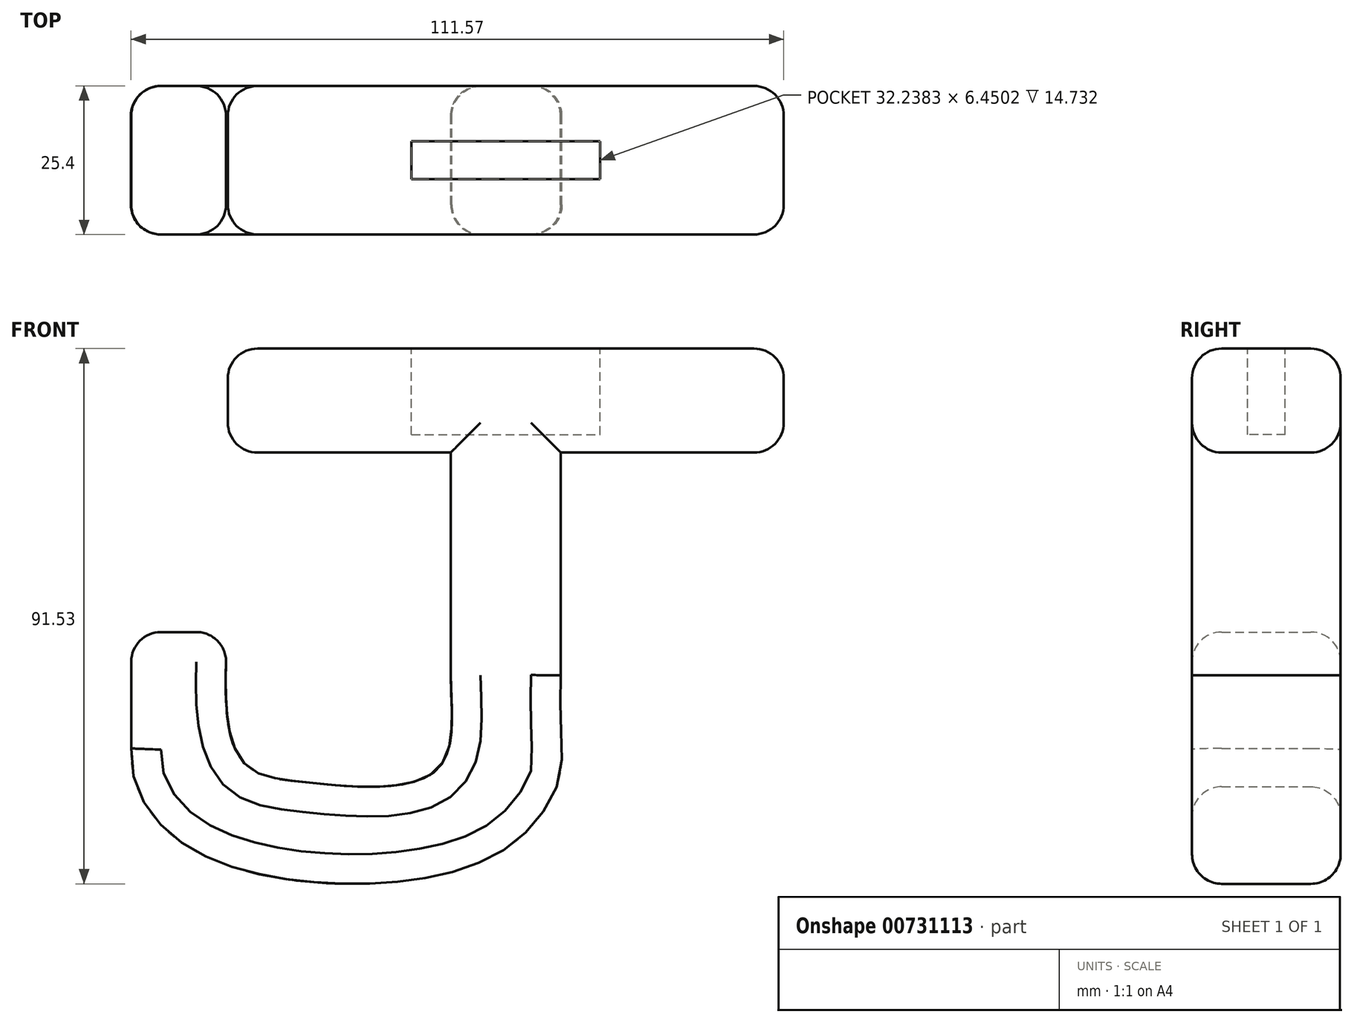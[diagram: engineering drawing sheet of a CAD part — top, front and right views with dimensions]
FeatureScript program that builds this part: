
annotation { "Feature Type Name" : "Feature", "Feature Type Description" : "" }
export const myFeature = defineFeature(function(context is Context, id is Id, definition is map)
    precondition{}
    {
        {
            var Q0;
            Q0=qCreatedBy(makeId("Front.planeOp"),FACE);
            var sketch = newSketch(context, id + "F0", { "sketchPlane" : qUnion([Q0])});
            skLineSegment(sketch, "E0", {"start": v(-64.85, 45.6) * mm, "end": v(-26.75, 45.6) * mm});
            skLineSegment(sketch, "E1", {"start": v(-64.85, 45.6) * mm, "end": v(-64.85, 27.82) * mm});
            skLineSegment(sketch, "E2", {"start": v(-64.85, 27.82) * mm, "end": v(-26.75, 27.82) * mm});
            skLineSegment(sketch, "E3", {"start": v(-26.75, 27.82) * mm, "end": v(-26.75, -10.29) * mm});
            skFitSpline(sketch, "E4", {"points": [v(-26.75, -10.29) * mm, v(-29.03, -26.34) * mm, v(-52.79, -28.42) * mm, v(-64.85, -2.87) * mm], "startDerivative": vector(0, -55.22) * mm, "endDerivative": vector(14.79, 193.6) * mm});
            skLineSegment(sketch, "E5", {"start": v(-64.85, -2.87) * mm, "end": v(-81.36, -2.87) * mm});
            skLineSegment(sketch, "E6", {"start": v(-81.36, -2.87) * mm, "end": v(-81.36, -22.78) * mm});
            skFitSpline(sketch, "E7", {"points": [v(-81.36, -22.78) * mm, v(-73.83, -38.08) * mm, v(-46.17, -45.89) * mm, v(-17.3, -39.87) * mm, v(-8.27, -28.42) * mm, v(-7.94, -10.29) * mm], "startDerivative": vector(-7.77, -94.3) * mm, "endDerivative": vector(5.43, 211.23) * mm});
            skLineSegment(sketch, "E8", {"start": v(-7.94, -10.29) * mm, "end": v(-7.94, 27.82) * mm});
            skLineSegment(sketch, "E9", {"start": v(-7.94, 27.82) * mm, "end": v(30.16, 27.82) * mm});
            skLineSegment(sketch, "E10", {"start": v(30.16, 27.82) * mm, "end": v(30.16, 45.6) * mm});
            skLineSegment(sketch, "E11", {"start": v(30.16, 45.6) * mm, "end": v(-26.75, 45.6) * mm});
            skPoint(sketch, "E12", {"position": v(-7.94, 45.6) * mm});
            skLineSegment(sketch, "E13.bottom", {"start": v(-26.75, 45.6) * mm, "end": v(-7.94, 45.6) * mm});
            skSolve(sketch);
        }
        {
            var Q0;
            Q0=makeQuery(id+"F0.imprint","IMPRINT",FACE,{"disambiguationData":[TD([[makeQuery(id+"F0.imprint","IMPRINT",EDGE,{"derivedFrom":sQuery(id+"F0.wireOp",EDGE,"E0")}),-1.0]])]});
            extrude(context, id + "F1", {"entities" : qUnion([Q0]), "depth" : 25.4 * mm, "offsetDistance" : 25.4 * mm});
        }
        {
            var Q0;
            Q0=makeQuery(id+"F1.opExtrude","CAP_FACE",FACE,{"disambiguationData":[OSD([sQuery(id+"F0.wireOp",EDGE,"E0"),sQuery(id+"F0.wireOp",EDGE,"E1"),sQuery(id+"F0.wireOp",EDGE,"E2"),sQuery(id+"F0.wireOp",EDGE,"E3"),sQuery(id+"F0.wireOp",EDGE,"E4"),sQuery(id+"F0.wireOp",EDGE,"E5"),sQuery(id+"F0.wireOp",EDGE,"E6"),sQuery(id+"F0.wireOp",EDGE,"E7"),sQuery(id+"F0.wireOp",EDGE,"E8"),sQuery(id+"F0.wireOp",EDGE,"E9"),sQuery(id+"F0.wireOp",EDGE,"E10"),sQuery(id+"F0.wireOp",EDGE,"E11")])],"isStart":false});
            var Q1;
            Q1=makeQuery(id+"F1.opExtrude","CAP_EDGE",EDGE,{"disambiguationData":[OSD([sQuery(id+"F0.wireOp",EDGE,"E0"),sQuery(id+"F0.wireOp",EDGE,"E11")])],"isStart":true});
            var Q2;
            Q2=makeQuery(id+"F1.opExtrude","CAP_FACE",FACE,{"disambiguationData":[OSD([sQuery(id+"F0.wireOp",EDGE,"E0"),sQuery(id+"F0.wireOp",EDGE,"E1"),sQuery(id+"F0.wireOp",EDGE,"E2"),sQuery(id+"F0.wireOp",EDGE,"E3"),sQuery(id+"F0.wireOp",EDGE,"E4"),sQuery(id+"F0.wireOp",EDGE,"E5"),sQuery(id+"F0.wireOp",EDGE,"E6"),sQuery(id+"F0.wireOp",EDGE,"E7"),sQuery(id+"F0.wireOp",EDGE,"E8"),sQuery(id+"F0.wireOp",EDGE,"E9"),sQuery(id+"F0.wireOp",EDGE,"E10"),sQuery(id+"F0.wireOp",EDGE,"E11")])],"isStart":true});
            var Q3;
            Q3=makeQuery(id+"F1.opExtrude","SWEPT_FACE",FACE,{"disambiguationData":[OSD([sQuery(id+"F0.wireOp",EDGE,"E1")])]});
            var Q4;
            Q4=makeQuery(id+"F1.opExtrude","SWEPT_FACE",FACE,{"disambiguationData":[OSD([sQuery(id+"F0.wireOp",EDGE,"E5")])]});
            var Q5;
            Q5=makeQuery(id+"F1.opExtrude","SWEPT_FACE",FACE,{"disambiguationData":[OSD([sQuery(id+"F0.wireOp",EDGE,"E10")])]});
            fillet(context, id + "F2", {"entities" : qUnion([Q0, Q1, Q2, Q3, Q4, Q5]), "radius" : 5.08 * mm, "tangentPropagation" : true, "allowEdgeOverflow" : false});
        }
        {
            var Q0;
            Q0=makeQuery(id+"F1.opExtrude","SWEPT_FACE",FACE,{"disambiguationData":[OSD([sQuery(id+"F0.wireOp",EDGE,"E0"),sQuery(id+"F0.wireOp",EDGE,"E11"),sQuery(id+"F0.wireOp",EDGE,"E13.bottom")])]});
            var sketch = newSketch(context, id + "F3", { "sketchPlane" : qUnion([Q0])});
            skLineSegment(sketch, "E14.bottom", {"start": v(-33.46, -9.47) * mm, "end": v(-1.22, -9.47) * mm});
            skLineSegment(sketch, "E14.top", {"start": v(-33.46, -15.93) * mm, "end": v(-1.22, -15.93) * mm});
            skLineSegment(sketch, "E14.left", {"start": v(-33.46, -9.47) * mm, "end": v(-33.46, -15.93) * mm});
            skLineSegment(sketch, "E14.right", {"start": v(-1.22, -9.47) * mm, "end": v(-1.22, -15.93) * mm});
            skPoint(sketch, "E14.middle", {"position": v(-17.34, -12.7) * mm});
            skPoint(sketch, "E14.middle.positionSnap0", {"position": v(25.08, -12.7) * mm});
            skPoint(sketch, "E14.middle.positionSnap1", {"position": v(-17.34, -5.08) * mm});
            skPoint(sketch, "E14.centerSnap0", {"position": v(25.08, -12.7) * mm});
            skPoint(sketch, "E14.centerSnap1", {"position": v(-17.34, -5.08) * mm});
            skSolve(sketch);
        }
        {
            var Q0;
            Q0=makeQuery(id+"F3.imprint","IMPRINT",FACE,{"disambiguationData":[TD([[makeQuery(id+"F3.imprint","IMPRINT",EDGE,{"derivedFrom":sQuery(id+"F3.wireOp",EDGE,"E14.bottom")}),-1.0]])]});
            extrude(context, id + "F4", {"entities" : qUnion([Q0]), "operationType" : NewBodyOperationType.REMOVE, "oppositeDirection" : true, "depth" : 14.73 * mm, "offsetDistance" : 25.4 * mm});
        }
    });
